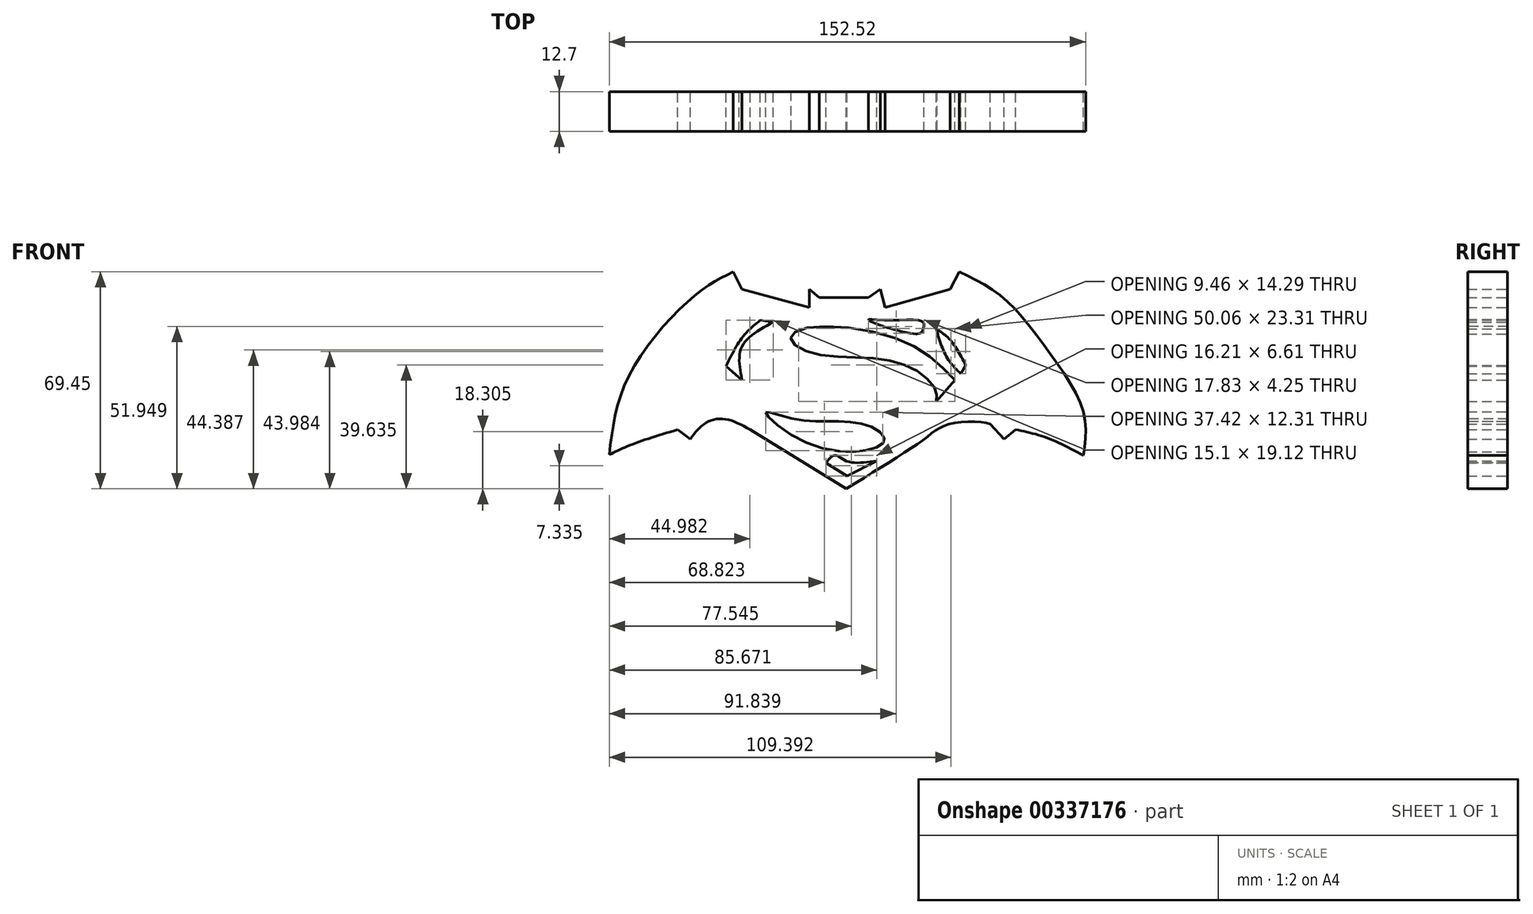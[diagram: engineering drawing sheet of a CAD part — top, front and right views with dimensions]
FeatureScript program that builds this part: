
annotation { "Feature Type Name" : "Feature", "Feature Type Description" : "" }
export const myFeature = defineFeature(function(context is Context, id is Id, definition is map)
    precondition{}
    {
        {
            var Q0;
            Q0=qCreatedBy(makeId("Front.planeOp"),FACE);
            var sketch = newSketch(context, id + "F0", { "sketchPlane" : qUnion([Q0])});
            skFitSpline(sketch, "E0", {"points": [v(-76.08, -13.59) * mm, v(-69.85, 11.57) * mm, v(-48.5, 37.54) * mm, v(-36.43, 44.99) * mm], "startDerivative": vector(8.28, 71.32) * mm, "endDerivative": vector(43.45, 21.5) * mm});
            skFitSpline(sketch, "E1", {"points": [v(-36.43, 44.99) * mm, v(-33.61, 39.35) * mm], "startDerivative": vector(2.82, -5.64) * mm, "endDerivative": vector(2.82, -5.64) * mm});
            skFitSpline(sketch, "E2", {"points": [v(-33.61, 39.35) * mm, v(-12.08, 33.51) * mm], "startDerivative": vector(21.54, -5.84) * mm, "endDerivative": vector(21.54, -5.84) * mm});
            skFitSpline(sketch, "E3", {"points": [v(-12.08, 33.51) * mm, v(-12.08, 39.35) * mm], "startDerivative": vector(0, 5.84) * mm, "endDerivative": vector(0, 5.84) * mm});
            skFitSpline(sketch, "E4", {"points": [v(-12.08, 39.35) * mm, v(-8.86, 36.73) * mm], "startDerivative": vector(3.22, -2.62) * mm, "endDerivative": vector(3.22, -2.62) * mm});
            skFitSpline(sketch, "E5", {"points": [v(-8.86, 36.73) * mm, v(6.84, 36.73) * mm], "startDerivative": vector(15.7, 0) * mm, "endDerivative": vector(15.7, 0) * mm});
            skFitSpline(sketch, "E6", {"points": [v(6.84, 36.73) * mm, v(10.67, 39.35) * mm], "startDerivative": vector(3.82, 2.62) * mm, "endDerivative": vector(3.82, 2.62) * mm});
            skFitSpline(sketch, "E7", {"points": [v(10.67, 39.35) * mm, v(12.28, 33.51) * mm], "startDerivative": vector(1.61, -5.84) * mm, "endDerivative": vector(1.61, -5.84) * mm});
            skFitSpline(sketch, "E8", {"points": [v(12.28, 33.51) * mm, v(33.01, 39.35) * mm], "startDerivative": vector(20.73, 5.84) * mm, "endDerivative": vector(20.73, 5.84) * mm});
            skFitSpline(sketch, "E9", {"points": [v(33.01, 39.35) * mm, v(36.03, 44.99) * mm], "startDerivative": vector(3.02, 5.64) * mm, "endDerivative": vector(3.02, 5.64) * mm});
            skFitSpline(sketch, "E10", {"points": [v(36.03, 44.99) * mm, v(49.92, 36.73) * mm, v(64.61, 19.42) * mm, v(75.7, 0) * mm, v(75.7, -13.79) * mm], "startDerivative": vector(61.01, -29.32) * mm, "endDerivative": vector(-8.9, -62.3) * mm});
            skFitSpline(sketch, "E11", {"points": [v(75.7, -13.79) * mm, v(64, -8.15) * mm, v(53.94, -5.54) * mm], "startDerivative": vector(-22.39, 12.04) * mm, "endDerivative": vector(-21.1, 4.33) * mm});
            skFitSpline(sketch, "E12", {"points": [v(53.94, -5.54) * mm, v(50.32, -8.55) * mm], "startDerivative": vector(-3.62, -3.02) * mm, "endDerivative": vector(-3.62, -3.02) * mm});
            skFitSpline(sketch, "E13", {"points": [v(50.32, -8.55) * mm, v(45.9, -3.72) * mm], "startDerivative": vector(-4.43, 4.83) * mm, "endDerivative": vector(-4.43, 4.83) * mm});
            skFitSpline(sketch, "E14", {"points": [v(47.37, -5.33) * mm, v(45.9, -3.72) * mm, v(33.01, -3.72) * mm, v(24.76, -8.55) * mm, v(-0.2, -24.46) * mm], "startDerivative": vector(-7.1, 16.4) * mm, "endDerivative": vector(-73.23, -44.58) * mm});
            skFitSpline(sketch, "E15", {"points": [v(-0.2, -24.46) * mm, v(-31, -5.54) * mm], "startDerivative": vector(-30.8, 18.92) * mm, "endDerivative": vector(-30.8, 18.92) * mm});
            skFitSpline(sketch, "E16", {"points": [v(-31, -5.54) * mm, v(-39.45, -2.11) * mm, v(-45.7, -3.72) * mm, v(-50.12, -8.55) * mm], "startDerivative": vector(-23.1, 12.6) * mm, "endDerivative": vector(-12.64, -17.16) * mm});
            skFitSpline(sketch, "E17", {"points": [v(-50.12, -8.55) * mm, v(-54.15, -5.54) * mm], "startDerivative": vector(-4.03, 3.02) * mm, "endDerivative": vector(-4.03, 3.02) * mm});
            skFitSpline(sketch, "E18", {"points": [v(-54.15, -5.54) * mm, v(-69.04, -10.37) * mm, v(-76.08, -13.59) * mm], "startDerivative": vector(-27.81, -8.35) * mm, "endDerivative": vector(-15.35, -7.71) * mm});
            skFitSpline(sketch, "E19", {"points": [v(-23.55, 28.88) * mm, v(-33.61, 21.03) * mm, v(-33.61, 10.37) * mm], "startDerivative": vector(-24.3, -13.12) * mm, "endDerivative": vector(4.6, -24.08) * mm});
            skFitSpline(sketch, "E20", {"points": [v(-33.61, 10.37) * mm, v(-38.65, 14.8) * mm], "startDerivative": vector(-5.03, 4.43) * mm, "endDerivative": vector(-5.03, 4.43) * mm});
            skFitSpline(sketch, "E21", {"points": [v(-38.65, 14.8) * mm, v(-33.61, 23.85) * mm, v(-27.78, 29.49) * mm], "startDerivative": vector(8.7, 18.42) * mm, "endDerivative": vector(13.12, 10.82) * mm});
            skFitSpline(sketch, "E22", {"points": [v(-27.78, 29.49) * mm, v(-23.55, 28.88) * mm], "startDerivative": vector(4.23, -0.6) * mm, "endDerivative": vector(4.23, -0.6) * mm});
            skFitSpline(sketch, "E23", {"points": [v(6.84, 29.49) * mm, v(22.54, 25.06) * mm, v(24.36, 26.6) * mm, v(24.36, 28.88) * mm, v(12.28, 29.49) * mm, v(6.84, 29.49) * mm]});
            skFitSpline(sketch, "E24", {"points": [v(28.58, 26.67) * mm, v(32, 17.61) * mm, v(36.43, 12.38) * mm], "startDerivative": vector(5.38, -18.1) * mm, "endDerivative": vector(10.47, -10.26) * mm});
            skFitSpline(sketch, "E25", {"points": [v(36.43, 12.38) * mm, v(38.04, 15) * mm], "startDerivative": vector(1.61, 2.62) * mm, "endDerivative": vector(1.61, 2.62) * mm});
            skFitSpline(sketch, "E26", {"points": [v(38.04, 15) * mm, v(33.21, 23.05) * mm, v(28.58, 26.67) * mm], "startDerivative": vector(-8.14, 16.16) * mm, "endDerivative": vector(-10.88, 6.83) * mm});
            skFitSpline(sketch, "E27", {"points": [v(28.58, 3.52) * mm, v(34.62, 10.37) * mm], "startDerivative": vector(6.04, 6.84) * mm, "endDerivative": vector(6.04, 6.84) * mm});
            skFitSpline(sketch, "E28", {"points": [v(34.62, 10.37) * mm, v(16.5, 23.4) * mm, v(-14.5, 26.67) * mm, v(-17.91, 23.4) * mm, v(-10.67, 18.82) * mm, v(9.46, 17.2) * mm, v(23.75, 12.38) * mm, v(28.58, 6.54) * mm, v(28.58, 3.52) * mm], "startDerivative": vector(-87.6, 88.25) * mm, "endDerivative": vector(-8.15, -46.15) * mm});
            skFitSpline(sketch, "E29", {"points": [v(-25.97, 0) * mm, v(-13.49, -9.56) * mm, v(7.65, -11.84) * mm, v(12.08, -8.76) * mm, v(7.04, -4.33) * mm, v(-5.23, -2.92) * mm, v(-18.92, -1.71) * mm, v(-25.97, 0) * mm]});
            skFitSpline(sketch, "E30", {"points": [v(-6.64, -16.2) * mm, v(0, -20.43) * mm], "startDerivative": vector(6.64, -4.23) * mm, "endDerivative": vector(6.64, -4.23) * mm});
            skFitSpline(sketch, "E31", {"points": [v(0, -20.43) * mm, v(9.57, -15.6) * mm], "startDerivative": vector(9.57, 4.83) * mm, "endDerivative": vector(9.57, 4.83) * mm});
            skFitSpline(sketch, "E32", {"points": [v(9.57, -15.6) * mm, v(-0.2, -15.6) * mm, v(-3.82, -13.79) * mm, v(-6.64, -16.2) * mm], "startDerivative": vector(-24.87, -3.28) * mm, "endDerivative": vector(-10.19, -13.1) * mm});
            skSolve(sketch);
        }
        {
            var Q0;
            Q0 = qSketchRegion(id + "F0", true);
            extrude(context, id + "F1", {"entities" : qUnion([Q0]), "depth" : 12.7 * mm});
        }
    });
